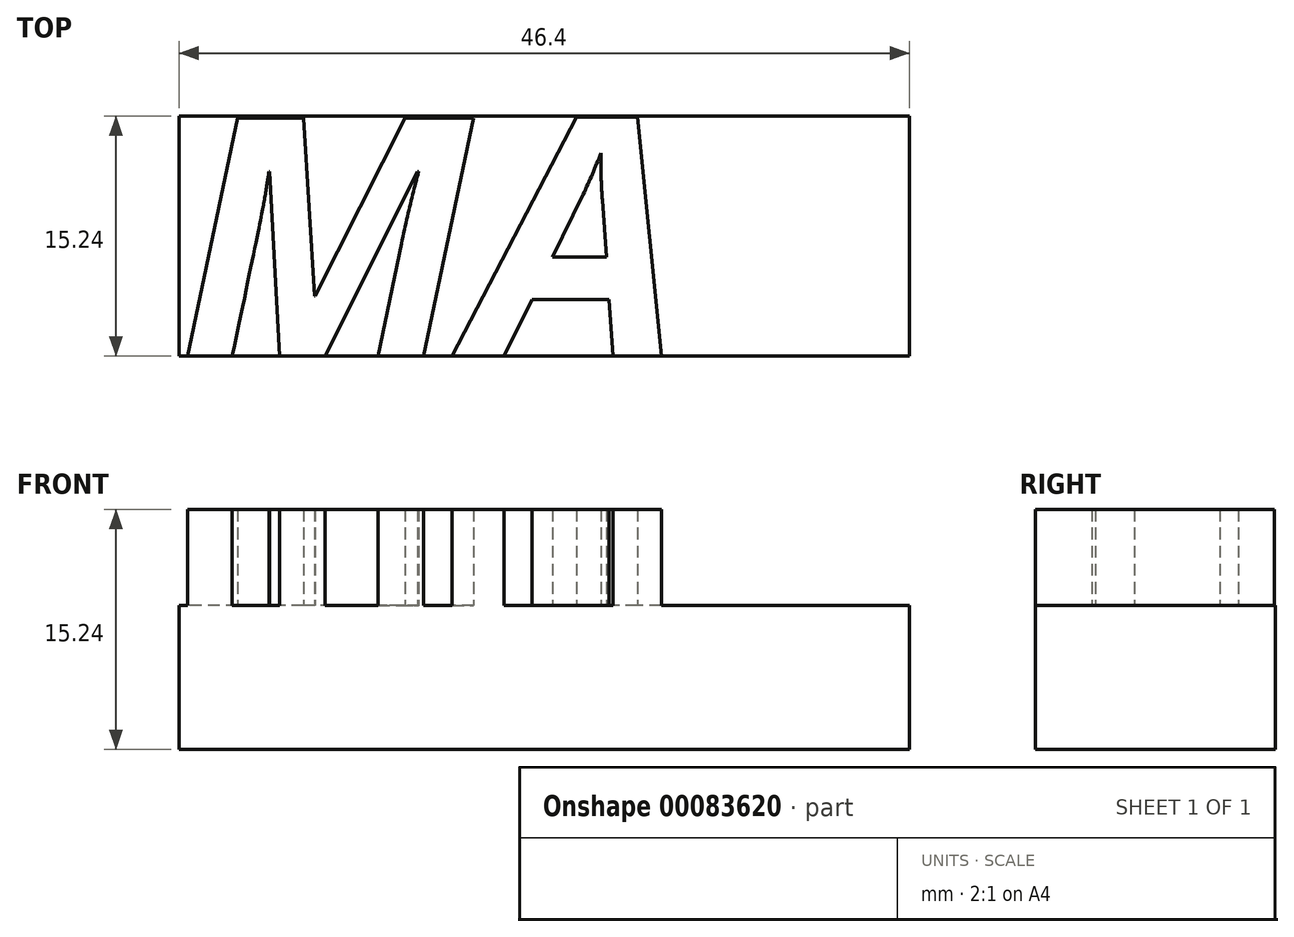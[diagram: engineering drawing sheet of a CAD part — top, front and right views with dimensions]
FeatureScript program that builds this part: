
annotation { "Feature Type Name" : "Feature", "Feature Type Description" : "" }
export const myFeature = defineFeature(function(context is Context, id is Id, definition is map)
    precondition{}
    {
        {
            var Q0;
            Q0=qCreatedBy(makeId("Top.planeOp"),FACE);
            var sketch = newSketch(context, id + "F0", { "sketchPlane" : qUnion([Q0])});
            skLineSegment(sketch, "E0.bottom", {"start": v(-23.2, -7.62) * mm, "end": v(23.2, -7.62) * mm});
            skLineSegment(sketch, "E0.top", {"start": v(-23.2, 7.62) * mm, "end": v(23.2, 7.62) * mm});
            skLineSegment(sketch, "E0.left", {"start": v(-23.2, -7.62) * mm, "end": v(-23.2, 7.62) * mm});
            skLineSegment(sketch, "E0.right", {"start": v(23.2, -7.62) * mm, "end": v(23.2, 7.62) * mm});
            skPoint(sketch, "E0.middle", {"position": v(0, 0) * mm});
            skText(sketch, "E1", { "text": "MAX", "fontName": "OpenSans-BoldItalic.ttf"});
            const initialGuessF0  = {"E1": [-0.0232, -0.00762, 1, 0, 0.01524]};
            skSetInitialGuess(sketch, initialGuessF0);
            skSolve(sketch);
        }
        {
            var Q0;
            Q0 = qSketchRegion(id + "F0", true);
            var Q1;
            Q1=makeQuery(id+"F0.imprint","IMPRINT",FACE,{"disambiguationData":[TD([[makeQuery(id+"F0.imprint","IMPRINT",EDGE,{"derivedFrom":sQuery(id+"F0.wireOp",EDGE,"E1.sketch_text.stroke-26")}),1.0]])]});
            extrude(context, id + "F1", {"entities" : qUnion([Q0, Q1]), "depth" : 9.14 * mm});
        }
        {
            var Q0;
            Q0=makeQuery(id+"F0.imprint","IMPRINT",FACE,{"disambiguationData":[TD([[makeQuery(id+"F0.imprint","IMPRINT",EDGE,{"derivedFrom":sQuery(id+"F0.wireOp",EDGE,"E1.sketch_text.stroke-0")}),-1.0]])]});
            var Q1;
            Q1=makeQuery(id+"F0.imprint","IMPRINT",FACE,{"disambiguationData":[TD([[makeQuery(id+"F0.imprint","IMPRINT",EDGE,{"derivedFrom":sQuery(id+"F0.wireOp",EDGE,"E1.sketch_text.stroke-18")}),-1.0]])]});
            var Q2;
            Q2=makeQuery(id+"F0.imprint","IMPRINT",FACE,{"disambiguationData":[TD([[makeQuery(id+"F0.imprint","IMPRINT",EDGE,{"derivedFrom":sQuery(id+"F0.wireOp",EDGE,"E1.sketch_text.stroke-32")}),-1.0]])]});
            extrude(context, id + "F2", {"entities" : qUnion([Q0, Q1, Q2]), "operationType" : NewBodyOperationType.ADD, "depth" : 15.24 * mm});
        }
    });
